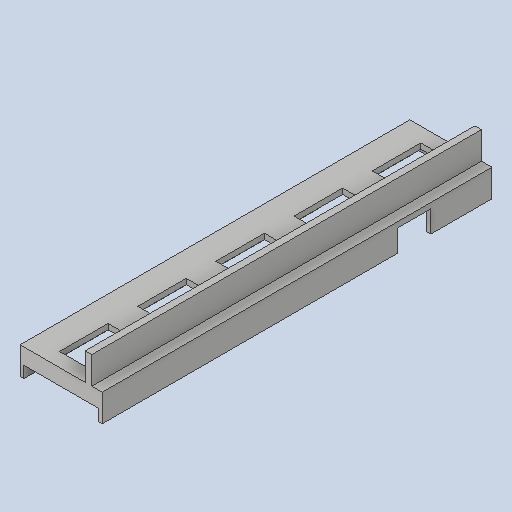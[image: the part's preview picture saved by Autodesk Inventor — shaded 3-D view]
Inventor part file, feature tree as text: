
AUTODESK INVENTOR PART (.ipt)
format: ipt  version: 2023 (Build 270158000, 158)  size: 195,072 bytes
history: native  units: mm
features: other x56, extrude x8, sketch x8
ambient origin geometry x8: Origin, YZ Plane, XZ Plane, XY Plane, X Axis, Y Axis, Z Axis, Center Point
bodies: Solid1 (feature_tree)
feature tree (72):
  extrude  "Extrusion1"  Depth=178.0mm TaperAngle=0.0deg
  extrude  "Extrusion2"  Depth=8.0mm TaperAngle=0.0deg
  extrude  "Extrusion3"  Depth=8.0mm TaperAngle=0.0deg
  extrude  "Extrusion4"  Depth=4.7mm TaperAngle=0.0deg
  extrude  "Extrusion5"  [1 undecoded]
  extrude  "Extrusion6"  [1 undecoded]
  extrude  "Extrusion7"  [1 undecoded]
  extrude  "Extrusion8"  [1 undecoded]
  other  "p_XY"
  other  "p_YZ"
  other  "p_ZX"
  other  "p_X"
  other  "p_Y"
  other  "p_Z"
  other  "p_Center"
  other  "p1_XY"
  other  "p1_YZ"
  other  "p1_ZX"
  other  "p1_X"
  other  "p1_Y"
  other  "p1_Z"
  other  "p1_Center"
  other  "p2_XY"
  other  "p2_YZ"
  other  "p2_ZX"
  other  "p2_X"
  other  "p2_Y"
  other  "p2_Z"
  other  "p2_Center"
  other  "p3_XY"
  other  "p3_YZ"
  other  "p3_ZX"
  other  "p3_X"
  other  "p3_Y"
  other  "p3_Z"
  other  "p3_Center"
  other  "p4_XY"
  other  "p4_YZ"
  other  "p4_ZX"
  other  "p4_X"
  other  "p4_Y"
  other  "p4_Z"
  other  "p4_Center"
  other  "p5_XY"
  other  "p5_YZ"
  other  "p5_ZX"
  other  "p5_X"
  other  "p5_Y"
  other  "p5_Z"
  other  "p5_Center"
  other  "p6_XY"
  other  "p6_YZ"
  other  "p6_ZX"
  other  "p6_X"
  other  "p6_Y"
  other  "p6_Z"
  other  "p6_Center"
  other  "p7_XY"
  other  "p7_YZ"
  other  "p7_ZX"
  other  "p7_X"
  other  "p7_Y"
  other  "p7_Z"
  other  "p7_Center"
  sketch  "Sketch_1"  dims[d0=178.0mm d1=0.0mm d2=8.0mm d3=0.0mm]
  sketch  "Sketch_2"  dims[d4=8.0mm d5=0.0mm d6=8.0mm d7=0.0mm]
  sketch  "Sketch_3"  dims[d8=8.0mm d9=0.0mm d10=8.0mm d11=0.0mm]
  sketch  "Sketch_4"  dims[d12=37.5mm d13=0.0mm d14=4.7mm d15=0.0mm]
  sketch  "Sketch_5"  dims[d16=0.0mm]
  sketch  "Sketch_6"
  sketch  "Sketch_10"
  sketch  "Sketch_13"
note: 4 required parameter values undecoded (feature->parameter linkage not recoverable at this tier; creation-order binding heuristic only, values carry confidence <= 0.55)
